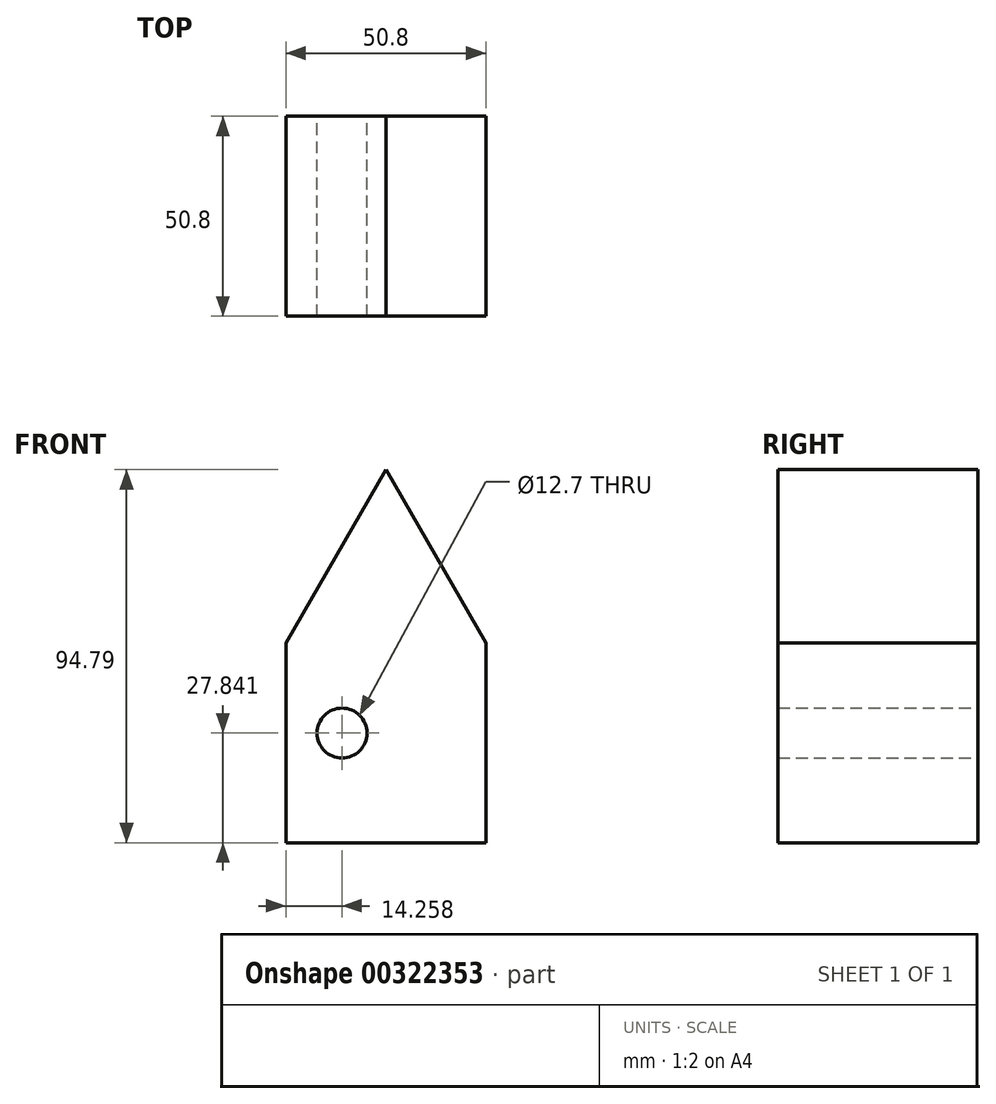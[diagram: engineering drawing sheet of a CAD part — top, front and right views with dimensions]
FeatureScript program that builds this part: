
annotation { "Feature Type Name" : "Feature", "Feature Type Description" : "" }
export const myFeature = defineFeature(function(context is Context, id is Id, definition is map)
    precondition{}
    {
        {
            var Q0;
            Q0=qCreatedBy(makeId("Front.planeOp"),FACE);
            var sketch = newSketch(context, id + "F0", { "sketchPlane" : qUnion([Q0])});
            skLineSegment(sketch, "E0.top", {"start": v(0, -50.8) * mm, "end": v(50.8, -50.8) * mm});
            skLineSegment(sketch, "E0.left", {"start": v(0, 0) * mm, "end": v(0, -50.8) * mm});
            skLineSegment(sketch, "E0.right", {"start": v(50.8, 0) * mm, "end": v(50.8, -50.8) * mm});
            skLineSegment(sketch, "E1", {"start": v(25.4, 44) * mm, "end": v(50.8, 0) * mm});
            skLineSegment(sketch, "E2", {"start": v(25.4, 44) * mm, "end": v(0, 0) * mm});
            skCircle(sketch, "E3", {"center": v(14.26, -22.96) * mm, "radius": 6.35 * mm});
            skSolve(sketch);
        }
        {
            var Q0;
            Q0 = qSketchRegion(id + "F0", true);
            extrude(context, id + "F1", {"entities" : qUnion([Q0]), "depth" : 50.8 * mm});
        }
    });
